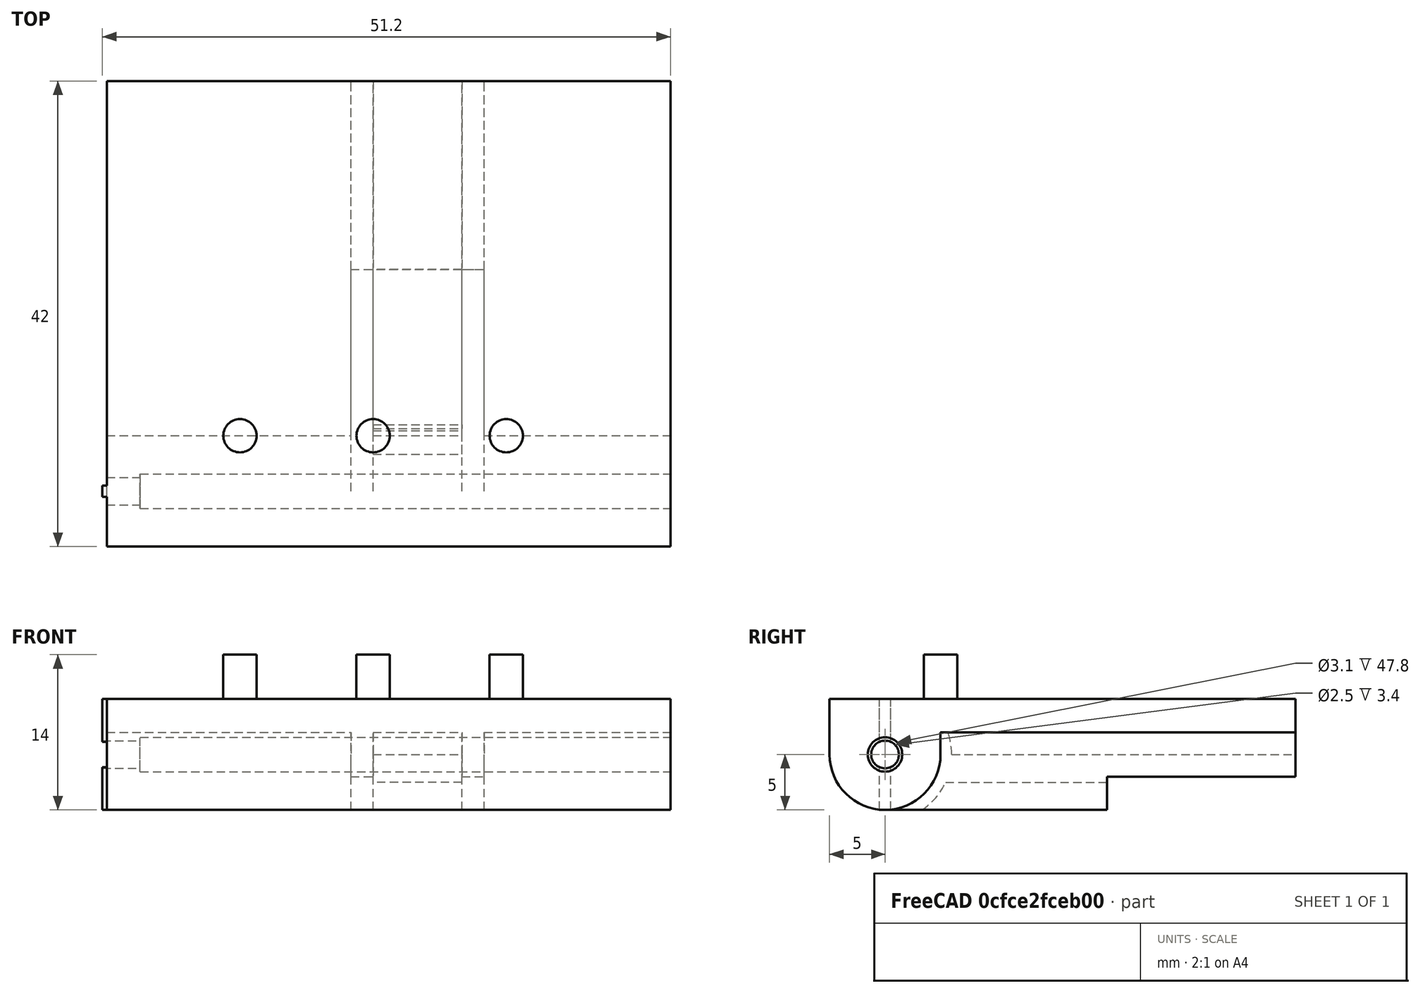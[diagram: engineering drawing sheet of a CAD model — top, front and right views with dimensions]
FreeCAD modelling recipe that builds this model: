
FCSTD DOCUMENT  (FreeCAD 0.16R6707 (Git))
Label: xmaxx-bumber-left
License: All rights reserved
LicenseURL: http://en.wikipedia.org/wiki/All_rights_reserved
objects: Part::Cylinder×7, Part::Box×6, Part::Cut×5, Part::MultiFuse×4
note: 22 computed .brp shape members not serialized (recipe doc carries the construction recipe); baked Part::Feature solids carry a one-line shape summary decoded from their .brp

FEATURE [Part::Box] Box  label="Cube"
  Height = 3
  Length = 50.8
  Width = 42
FEATURE [Part::Box] Box001  label="Cube001"
  Height = 2
  Length = 50.8
  Placement = pos=(0,0,-2) rot=(0,0,1;0rad)
  Width = 10
FEATURE [Part::Cylinder] Cylinder
  Angle = 360
  Height = 50.8
  Placement = pos=(0,5,-2) rot=(0,1,0;1.5708rad)
  Radius = 5
FEATURE [Part::Cylinder] Cylinder001
  Angle = 360
  Height = 50.8
  Placement = pos=(3,5,-2) rot=(0,1,0;1.5708rad)
  Radius = 1.55
FEATURE [Part::Cylinder] Cylinder002
  Angle = 360
  Height = 10
  Placement = pos=(-1,5,-2) rot=(0,1,0;1.5708rad)
  Radius = 1.25
FEATURE [Part::Box] Box002  label="Cube002"
  Height = 10
  Length = 0.4
  Placement = pos=(-0.4,4.5,-7) rot=(0,0,1;0rad)
  Width = 1
FEATURE [Part::Box] Box003  label="Cube003"
  Height = 10
  Length = 12
  Placement = pos=(22,5,-7) rot=(0,0,1;0rad)
  Width = 37
FEATURE [Part::Box] Box004  label="Cube004"
  Height = 2.5
  Length = 8
  Placement = pos=(24,10,-4.5) rot=(0,0,1;0rad)
  Width = 50
FEATURE [Part::Box] Box005  label="Cube005"
  Height = 3
  Length = 12
  Placement = pos=(22,25,-7) rot=(0,0,1;0rad)
  Width = 18
FEATURE [Part::Cut] Cut
  Base = -> Box003
  Tool = -> Box004
FEATURE [Part::Cut] Cut001
  Base = -> Cut
  Tool = -> Box005
FEATURE [Part::Cylinder] Cylinder003
  Angle = 360
  Height = 8
  Placement = pos=(24,5,-2) rot=(0,1,0;1.5708rad)
  Radius = 6
FEATURE [Part::Cut] Cut002
  Base = -> Cut001
  Tool = -> Cylinder003
FEATURE [Part::MultiFuse] Fusion
  Shapes = -> [Box,Box001,Cylinder]
FEATURE [Part::MultiFuse] Fusion001
  Shapes = -> [Fusion,Box002]
FEATURE [Part::MultiFuse] Fusion002
  Shapes = -> [Fusion001,Cut002]
FEATURE [Part::Cut] Cut003
  Base = -> Fusion002
  Tool = -> Cylinder001
FEATURE [Part::Cut] Cut004
  Base = -> Cut003
  Tool = -> Cylinder002
FEATURE [Part::Cylinder] Cylinder004
  Angle = 360
  Height = 4
  Placement = pos=(12,10,3) rot=(0,0,1;0rad)
  Radius = 1.5
FEATURE [Part::Cylinder] Cylinder005
  Angle = 360
  Height = 4
  Placement = pos=(24,10,3) rot=(0,0,1;0rad)
  Radius = 1.5
FEATURE [Part::Cylinder] Cylinder006
  Angle = 360
  Height = 4
  Placement = pos=(36,10,3) rot=(0,0,1;0rad)
  Radius = 1.5
FEATURE [Part::MultiFuse] Fusion003
  Shapes = -> [Cut004,Cylinder004,Cylinder005,Cylinder006]
